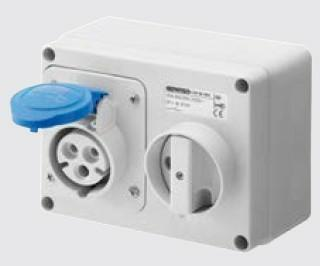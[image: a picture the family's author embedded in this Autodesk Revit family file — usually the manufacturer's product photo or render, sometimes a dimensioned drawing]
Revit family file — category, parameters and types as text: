
# Revit family: Building-ConnessioniIEC309-GEWISS-44IB-PRESE-INTERBLOCCATE_IP44_CON_FONDO
name_source: partatom
category: Apparecchi elettrici
units: mm (PartAtom-declared; Revit-internal decimal feet)

## family parameters
Condiviso = No
Host = Superficie
Mantenere orientamento annotazione = Sì
Punto di calcolo locali = Sì
Quota connettore circolare = Usa diametro
Taglio con vuoti quando caricato = No
Tipo di parte = Normale

## types (22) — shared parameters
BLOCCO = B=C
Catalogo = BUILDING
Catalogo Serie = 44 IB
Codice Electrocod = 2220
Con fondo = Si
FORMULA = 1000 mm  [stored 3.28084 ft]
Frequenza = 50/60 Hz
Frequenza nominale (Hz) = 50/60 Hz
Glow Wire Test = 850 °C (Parti attive) - 650 °C (Parti passive)
Glow wire test: = 850 °C (Parti attive) - 650 °C (Parti passive)
Grado di protezione = IP44
IDF = dbca06ac-afbb-49c0-85ef-3e15d7b39cd4
IDT = 54ab296f-77ff-4020-be1a-67a03cbf098f
Immagine tipo = IP44Fondo.jpg
L = 155 mm  [stored 0.50853 ft]
N_poli = 1
POMELLO = bianco
PRESA = Giallo
Produttore = GEWISS S.p.A.
Prospetto di default = 1219 mm
Protezione = NO (SBF)
Resistenza agli urti = IK08
SEO = Presa
STRUTTURA = RAL - 7035
STRUTTURA ALTA = blue
Scheda Tecnica = https://www.gewiss.com
Spostamento_S = 500 mm
Temperatura di funzionamento = -25 ÷ +40 °C
Temperatura di utilizzo = -25 +40 °C
Termopressione con biglia = 125 °C (Parti attive) - 80 °C (Parti passive)
Tipologia = Orizzontale
URL = https://www.gewiss.com
VETRO = Vetro
Versione file RFA = 21.4
Voltaggio = 0 V
W = 115 mm  [stored 0.377297 ft]

## per-type parameters (varying)
| type | Codice EAN | Colore | Colore: | Corrente nominale (A) | Corrente nominale (In) | Descrizione | Modello | N. poli | Numero di poli | Riferimento h | Tensione nominale |
| GW66002 - PRESA BL.OR.C.F.3P+T 16A 110V 4H SBF | 8011564005853 | Giallo | Giallo | 16 | 16 | PRESA BL.OR.C.F.3P+T 16A 110V 4H SBF | GW66002 | 3P+T | 3P+T | 4 | 100-130V |
| GW66008 - PRESA BL.OR.C.F.3P+T 16A 400V 6H SBF | 8011564005822 | Rosso | Rosso | 16 | 16 | PRESA BL.OR.C.F.3P+T 16A 400V 6H SBF | GW66008 | 3P+T | 3P+T | 6 | 380-415V |
| GW66017 - PRESA BL.OR.C.F.3P+N+T 32A 230V 9H SBF | 8011564006201 | Blu | Blu | 32 | 32 | PRESA BL.OR.C.F.3P+N+T 32A 230V 9H SBF | GW66017 | 3P+N+T | 3P+N+T | 9 | 200-250V |
| GW66021 - PRESA BL.OR.C.F.3P+T 32A 500V 7H SBF | 8011564006188 | Nero | Nero | 32 | 32 | PRESA BL.OR.C.F.3P+T 32A 500V 7H SBF | GW66021 | 3P+T | 3P+T | 7 | 480-500V |
| GW66005 - PRESA BL.OR.C.F.3P+T 16A 230V 9H SBF | 8011564005815 | Blu | Blu | 16 | 16 | PRESA BL.OR.C.F.3P+T 16A 230V 9H SBF | GW66005 | 3P+T | 3P+T | 9 | 200-250V |
| GW66015 - PRESA BL.OR.C.F.2P+T 32A 230V 6H SBF | 8011564006102 | Blu | Blu | 32 | 32 | PRESA BL.OR.C.F.2P+T 32A 230V 6H SBF | GW66015 | 2P+T | 2P+T | 6 | 200-250V |
| GW66020 - PRESA BL.OR.C.F.3P+N+T 32A 400V 6H SBF | 8011564006133 | Rosso | Rosso | 32 | 32 | PRESA BL.OR.C.F.3P+N+T 32A 400V 6H SBF | GW66020 | 3P+N+T | 3P+N+T | 6 | 380-415V |
| GW66007 - PRESA BL.OR.C.F.2P+T 16A 400V 9H SBF | 8011564005846 | Rosso | Rosso | 16 | 16 | PRESA BL.OR.C.F.2P+T 16A 400V 9H SBF | GW66007 | 2P+T | 2P+T | 9 | 380-415V |
| GW66012 - PRESA BL.OR.C.F.2P+T 32A 110V 4H SBF | 8011564006140 | Giallo | Giallo | 32 | 32 | PRESA BL.OR.C.F.2P+T 32A 110V 4H SBF | GW66012 | 2P+T | 2P+T | 4 | 100-130V |
| GW66001 - PRESA BL.OR.C.F.2P+T 16A 110V 4H SBF | 8011564005792 | Giallo | Giallo | 16 | 16 | PRESA BL.OR.C.F.2P+T 16A 110V 4H SBF | GW66001 | 2P+T | 2P+T | 4 | 100-130V |
| GW66011 - PRESA BL.OR.C.F.3P+N+T 16A 500V 7H SBF | 8011564006096 | Nero | Nero | 16 | 16 | PRESA BL.OR.C.F.3P+N+T 16A 500V 7H SBF | GW66011 | 3P+N+T | 3P+N+T | 7 | 480-500V |
| GW66009 - PRESA BL.OR.C.F.3P+N+T 16A 400V 6H SBF | 8011564005839 | Rosso | Rosso | 16 | 16 | PRESA BL.OR.C.F.3P+N+T 16A 400V 6H SBF | GW66009 | 3P+N+T | 3P+N+T | 6 | 380-415V |
| GW66013 - PRESA BL.OR.C.F.3P+T 32A 110V 4H SBF | 8011564006164 | Giallo | Giallo | 32 | 32 | PRESA BL.OR.C.F.3P+T 32A 110V 4H SBF | GW66013 | 3P+T | 3P+T | 4 | 100-130V |
| GW66019 - PRESA BL.OR.C.F.3P+T 32A 400V 6H SBF | 8011564006126 | Rosso | Rosso | 32 | 32 | PRESA BL.OR.C.F.3P+T 32A 400V 6H SBF | GW66019 | 3P+T | 3P+T | 6 | 380-415V |
| GW66006 - PRESA BL.OR.C.F.3P+N+T 16A 230V 9H SBF | 8011564005884 | Blu | Blu | 16 | 16 | PRESA BL.OR.C.F.3P+N+T 16A 230V 9H SBF | GW66006 | 3P+N+T | 3P+N+T | 9 | 200-250V |
| GW66018 - PRESA BL.OR.C.F.2P+T 32A 400V 9H SBF | 8011564006157 | Rosso | Rosso | 32 | 32 | PRESA BL.OR.C.F.2P+T 32A 400V 9H SBF | GW66018 | 2P+T | 2P+T | 9 | 380-415V |
| GW66003 - PRESA BL.OR.C.F.3P+N+T 16A 110V 4H SBF | 8011564005877 | Giallo | Giallo | 16 | 16 | PRESA BL.OR.C.F.3P+N+T 16A 110V 4H SBF | GW66003 | 3P+N+T | 3P+N+T | 4 | 100-130V |
| GW66022 - PRESA BL.OR.C.F.3P+N+T 32A 500V 7H SBF | 8011564006218 | Nero | Nero | 32 | 32 | PRESA BL.OR.C.F.3P+N+T 32A 500V 7H SBF | GW66022 | 3P+N+T | 3P+N+T | 7 | 480-500V |
| GW66010 - PRESA BL.OR.C.F.3P+T 16A 500V 7H SBF | 8011564005860 | Nero | Nero | 16 | 16 | PRESA BL.OR.C.F.3P+T 16A 500V 7H SBF | GW66010 | 3P+T | 3P+T | 7 | 480-500V |
| GW66016 - PRESA BL.OR.C.F.3P+T 32A 230V 9H SBF | 8011564006171 | Blu | Blu | 32 | 32 | PRESA BL.OR.C.F.3P+T 32A 230V 9H SBF | GW66016 | 3P+T | 3P+T | 9 | 200-250V |
| GW66004 - PRESA BL.OR.C.F.2P+T 16A 230V 6H SBF | 8011564005808 | Blu | Blu | 16 | 16 | PRESA BL.OR.C.F.2P+T 16A 230V 6H SBF | GW66004 | 2P+T | 2P+T | 6 | 200-250V |
| GW66014 - PRESA BL.OR.C.F.3P+N+T 32A 110V 4H SBF | 8011564006195 | Giallo | Giallo | 32 | 32 | PRESA BL.OR.C.F.3P+N+T 32A 110V 4H SBF | GW66014 | 3P+N+T | 3P+N+T | 4 | 100-130V |

note: [stored X ft] marks values corroborated as IEEE doubles in the binary element streams (Revit-internal decimal feet)

## geometry (parser evidence)
native form markers: Sweep x4
no freeform markers — native parametric forms only
